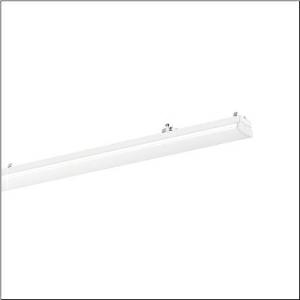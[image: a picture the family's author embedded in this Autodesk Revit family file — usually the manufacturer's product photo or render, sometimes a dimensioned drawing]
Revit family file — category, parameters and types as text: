
# Revit family: licross_r__21_recessed_opal_mo_52te1ddv495g_20cf
name_source: partatom
category: Lighting Fixtures
units: mm (PartAtom-declared; Revit-internal decimal feet)

## family parameters
Cut with Voids When Loaded = No
Host = Face
Light Source = No
Part Type = Normal
Room Calculation Point = No
Round Connector Dimension = Use Diameter
Shared = No

## types (1)
- --- (1 x LED, 9500 lm, 53.6 W, 4000K)
    Apparent Load = 54 VA
    CIE Flux Codes = 44 73 91 87 100
    Color Rendering = 80
    Color Temperature = 4000K
    Default Elevation = 1800 mm
    Description = Licross® 21 recessed opal MO, luminaire insert, of sheet steel, galvanised, coil coated, white, length: 2.250mm, width: 66mm, height: 67mm, LED rated luminous flux: 9.500lm, light colour: 840, control gear: DALI 2, with plug, 5-pole, with phase selection, mains connection: 220..240V, AC, 50/60Hz, rated input power: 54W, internal wiring halogen-free, primary optical cover: cover, of PMMA, light emission: direct with ceiling illumination distribution, primary light characteristic: symmetric, protection rating (complete): IP54, insulation class (complete): insulation class I (protective earthing), certification: CE, ENEC, VDE, UKCA, protection symbol: D if used in an environment with non-conductive dust loads with corresponding accessories, impact resistance: IK06, permissible ambient temperature for indoor applications: -25..+40°C, corresponds to IFS (International Featured Standards) requirements for safety and quality in the food industry, reducing of maximum allowable ambient temperature of 5°C with ceiling mounting, LABS conformity tested according to VDMA 24364:2018-05, packaging unit: 1 piece
    Height = 83 mm
    Lamp = 1 x LED
    Lamp Light Flux = 9500 lm
    Lamp Power = 53.6 W
    Lamp count = 1
    Length = 2250 mm
    Luminous efficacy = 177 lm/W
    Manufacturer = Siteco
    ModVariant = No
    Model = 52TE1DDV495G
    Mounting Place = Ceiling
    Mounting Type = Pendant
    Number of Poles = 1
    OnlyDefault = Yes
    Power Factor = 1
    Product Name = Licross® 21 recessed opal MO
    Product group = luminaire insert | ceiling pendant
    ProductGroupID = 902
    Protection Class = Protection class I
    Protection Degree = IP 54
    RLX_Detail_Level = 1
    RLX_Emergency_Light_Flux = 0 lm
    RLX_Emergency_Type = 0
    RLX_Emergency_Type_DB = No
    RlxData = <blob elided: 26461 chars, md5=e3c855eb>
    Socket = socket
    Standby Power = 0 W
    System Light Flux = 9500 lm
    System Power = 54 W
    Type Comments = factory setting: luminous flux: 100 % | dim-lin: 254 | 246 mA
    Type Image = l_1313666.jpg
    URL = http://relux.com
    VarID = @adj_086085
    Voltage = 0 V
    Weight = 0.00 kg
    Width = 76 mm

## geometry (parser evidence)
native form markers: Blend x4, Sweep x12
no freeform markers — native parametric forms only
